# Revit family: led_t8_batten_1200mm_38w_3000k_ct_140063304
name_source: partatom
category: Leuchten
revit_build: Autodesk Revit 2016 (Build: 20190508_0715(x64)
units: mm (PartAtom-declared; Revit-internal decimal feet)

## family parameters
Basisbauteil = Fläche
Beim Laden mit Abzugskörper schneiden = Nein
Bemaßung runder Anschluss = Durchmesser verwenden
Gemeinsam genutzt = Nein
Lichtquelle = Nein
Raumberechnungspunkt = Nein
Teiletyp = Normal

## types (1)
- LED T8 Batten 1200mm 38W 3000K CT (1 x LED, 3800 lm)
    Approval mark = CE
    Beschreibung = Linear LED batten with uniform light output. Delivered with clips for surface mounted installation. Suspension possible with separate accessory kit. Mechanically connect multiple luminaires via connector accessory. Energy saving up to 55%.
    CIE Flux Codes = 41 70 89 88 100
    Control Gear = Electronic ballast
    Height = 37 mm
    Hersteller = OPPLE
    Lamp Light Flux = 3800 lm
    Lamp count = 1
    Lampe = 1 x LED
    Length = 1200 mm
    Luminous efficacy = 100 lm/W
    ModVariant = Nein
    Modell = 140063304
    Mounting Place = Wall
    Mounting Type = Surface mounted
    Number of Poles = 1
    OnlyDefault = Ja
    Power Factor = 1
    Product Name = LED T8 Batten 1200mm 38W 3000K CT
    Product group = T8 Batten
    ProductGroupID = 2012
    Protection Class = Protection class I
    Protection Degree = IP 20
    RLX_Detail_Level = 1
    RlxData = <blob elided: 19453 chars, md5=864f9e50>
    Scheinlast = 38 VA
    Socket = socket
    Standby Power = 0 W
    System Light Flux = 3800 lm
    System Power = 38 W
    Typenbild = 140063304.jpg
    Typenkommentare = Product without accessories
    URL = http://relux.com
    VarID = ---
    Voltage = 0 V
    Vorgabe-Ansicht = 1800 mm
    Weight = 0.00 kg
    Width = 50 mm

## geometry (parser evidence)
native form markers: Blend x4, Sweep x12
no freeform markers — native parametric forms only
